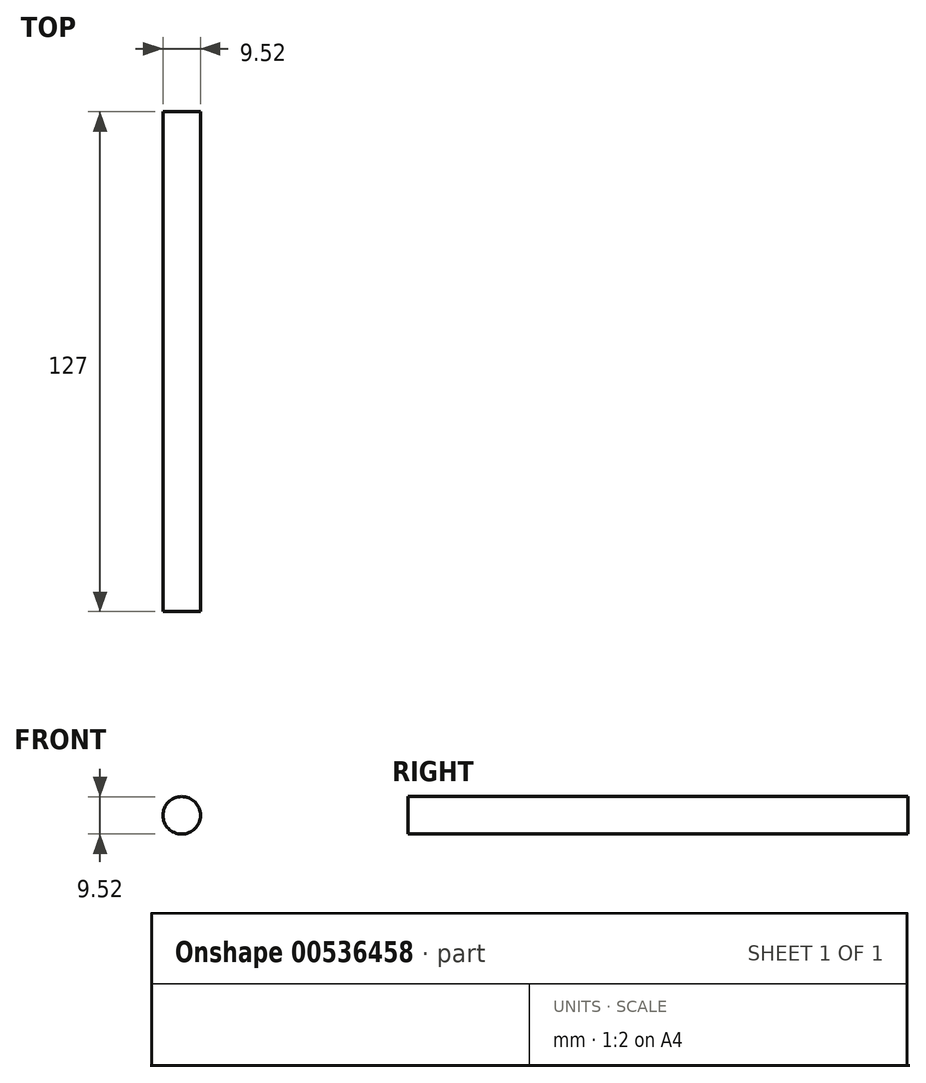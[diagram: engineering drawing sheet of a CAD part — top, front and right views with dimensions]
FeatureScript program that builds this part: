
annotation { "Feature Type Name" : "Feature", "Feature Type Description" : "" }
export const myFeature = defineFeature(function(context is Context, id is Id, definition is map)
    precondition{}
    {
        {
            var Q0;
            Q0=qCreatedBy(makeId("Front.planeOp"),FACE);
            var sketch = newSketch(context, id + "F0", { "sketchPlane" : qUnion([Q0])});
            skCircle(sketch, "E0", {"center": v(2.74, 7.53) * mm, "radius": 4.76 * mm});
            skSolve(sketch);
        }
        {
            var Q0;
            Q0 = qSketchRegion(id + "F0", true);
            extrude(context, id + "F1", {"entities" : qUnion([Q0]), "depth" : 127 * mm, "offsetDistance" : 25.4 * mm});
        }
    });
